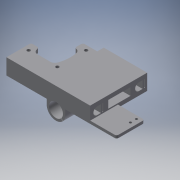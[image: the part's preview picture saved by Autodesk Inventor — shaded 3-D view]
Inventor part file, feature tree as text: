
AUTODESK INVENTOR PART (.ipt)
format: ipt  version: 2016 (Build 200138000, 138)  size: 1,464,320 bytes
history: native  units: mm
features: other x2, extrude x1, delete_face x1, sketch x1, projected_geometry x1
ambient origin geometry x8: Origin, YZ Plane, XZ Plane, XY Plane, X Axis, Y Axis, Z Axis, Center Point
bodies: Solid1 (feature_tree)
feature tree (6):
  other  "z-left_printer_1"
  other  "MeshFeature1"
  extrude  "Extrusion1"  [1 undecoded]
  delete_face  "Delete Face1"
  sketch  "Sketch1"  dims[d0=44.25mm d1=0.0mm]
  projected_geometry  "Projected Loop1"
note: 1 required parameter value undecoded (feature->parameter linkage not recoverable at this tier; creation-order binding heuristic only, values carry confidence <= 0.55)
